# Revit family: 306_bb9c2a21bfbd4a688d0d3089b44ac4
name_source: partatom
category: Pipe Accessories
units: mm (PartAtom-declared; Revit-internal decimal feet)

## family parameters
Always vertical = Yes
Cut with Voids When Loaded = No
Part Type = Valve - Breaks Into
Round Connector Dimension = Use Diameter
Shared = No
Work Plane-Based = No

## types (8) — shared parameters
CAT0 = Yes
Description = 2-way Fan coil valve VLG122, PN16 external thread
E = 16 mm  [stored 0.0524934 ft]
H1 = 23 mm  [stored 0.0754593 ft]
L2D = 38 mm  [stored 0.124672 ft]
L2D_Min = 3048 mm  [stored 10 ft]
Manufacturer = ESBE
QmdConnectorList = 301;D;302;D
R10 = 8 mm  [stored 0.0262467 ft]
R3 = 4 mm  [stored 0.0131234 ft]
R4 = 6 mm
R5 = 7 mm  [stored 0.0229659 ft]
R8 = 2 mm  [stored 0.00656168 ft]
R9 = 9 mm  [stored 0.0295276 ft]
URL = http://www.esbe.eu
W2D = 15 mm  [stored 0.0492126 ft]
X4 = 7 mm  [stored 0.0229659 ft]
X4__ve = -7 mm  [stored -0.0229659 ft]
Z2 = 5 mm  [stored 0.0164042 ft]
Z3 = 2 mm  [stored 0.00656168 ft]
Z5 = 9 mm  [stored 0.0295276 ft]
Z7 = 3 mm  [stored 0.00984252 ft]
Z7__ve = -3 mm
Z8 = 4 mm  [stored 0.0131234 ft]
magiPartTypeId = 306
magiProductFamilyId = bb9c2a21bfbd4a688d0d3089b44ac4

## per-type parameters (varying)
| type | C | D | DT2 | H | LT2 | MC Product Code | R1 | R2 | R6 | R7 | X3 | Z1 | magiProductId |
| VLG122 PN16 15-0,25 G1/2 | 23 mm  [stored 0.0754593 ft] | 15 mm | 8 mm  [stored 0.0262467 ft] | 27 mm  [stored 0.0885827 ft] | 19 mm  [stored 0.062336 ft] | VLG122 PN16 15-0,25 G1/2" | 7 mm  [stored 0.0229659 ft] | 13 mm | 11 mm | 15 mm  [stored 0.0492126 ft] | 34 mm  [stored 0.111549 ft] | 3 mm  [stored 0.00984252 ft] | 6cccb35838dc4c688cd3b564d69ed3 |
| VLG122 PN16 15-0,4 G1/2 | 23 mm  [stored 0.0754593 ft] | 15 mm | 8 mm  [stored 0.0262467 ft] | 27 mm  [stored 0.0885827 ft] | 19 mm  [stored 0.062336 ft] | VLG122 PN16 15-0,4 G1/2" | 7 mm  [stored 0.0229659 ft] | 13 mm | 11 mm | 15 mm  [stored 0.0492126 ft] | 34 mm  [stored 0.111549 ft] | 3 mm  [stored 0.00984252 ft] | 3b824731ee3a4ddb922e904129e44f |
| VLG122 PN16 15-0,6 G1/2 | 23 mm  [stored 0.0754593 ft] | 15 mm | 8 mm  [stored 0.0262467 ft] | 27 mm  [stored 0.0885827 ft] | 19 mm  [stored 0.062336 ft] | VLG122 PN16 15-0,6 G1/2" | 7 mm  [stored 0.0229659 ft] | 13 mm | 11 mm | 15 mm  [stored 0.0492126 ft] | 34 mm  [stored 0.111549 ft] | 3 mm  [stored 0.00984252 ft] | f23e7b00549f42fba3d46801f33b4e |
| VLG122 PN16 15-1,0 G1/2 | 23 mm  [stored 0.0754593 ft] | 15 mm | 8 mm  [stored 0.0262467 ft] | 27 mm  [stored 0.0885827 ft] | 19 mm  [stored 0.062336 ft] | VLG122 PN16 15-1,0 G1/2" | 7 mm  [stored 0.0229659 ft] | 13 mm | 11 mm | 15 mm  [stored 0.0492126 ft] | 34 mm  [stored 0.111549 ft] | 3 mm  [stored 0.00984252 ft] | 8756f888f78f4439910ff664cb444d |
| VLG122 PN16 15-1,6 G1/2 | 23 mm  [stored 0.0754593 ft] | 15 mm | 8 mm  [stored 0.0262467 ft] | 27 mm  [stored 0.0885827 ft] | 19 mm  [stored 0.062336 ft] | VLG122 PN16 15-1,6 G1/2" | 7 mm  [stored 0.0229659 ft] | 13 mm | 11 mm | 15 mm  [stored 0.0492126 ft] | 34 mm  [stored 0.111549 ft] | 3 mm  [stored 0.00984252 ft] | 5de91fdcf4d14890add016a982ef49 |
| VLG122 PN16 20-2,5 G3/4 | 24 mm  [stored 0.0787402 ft] | 20 mm | 10 mm  [stored 0.0328084 ft] | 26 mm  [stored 0.0853018 ft] | 21 mm  [stored 0.0688976 ft] | VLG122 PN16 20-2,5 G3/4" | 9 mm  [stored 0.0295276 ft] | 15 mm  [stored 0.0492126 ft] | 12 mm  [stored 0.0393701 ft] | 16 mm  [stored 0.0524934 ft] | 38 mm  [stored 0.124672 ft] | 4 mm  [stored 0.0131234 ft] | 3d202c79ad1e46bdb67021412b49dc |
| VLG122 PN16 20-4,0 G3/4 | 24 mm  [stored 0.0787402 ft] | 20 mm | 10 mm  [stored 0.0328084 ft] | 26 mm  [stored 0.0853018 ft] | 21 mm  [stored 0.0688976 ft] | VLG122 PN16 20-4,0 G3/4" | 9 mm  [stored 0.0295276 ft] | 15 mm  [stored 0.0492126 ft] | 12 mm  [stored 0.0393701 ft] | 16 mm  [stored 0.0524934 ft] | 38 mm  [stored 0.124672 ft] | 4 mm  [stored 0.0131234 ft] | aeef4dbbb471400997988208d80840 |
| VLG122 PN16 20-6,0 G3/4 | 24 mm  [stored 0.0787402 ft] | 20 mm | 10 mm  [stored 0.0328084 ft] | 26 mm  [stored 0.0853018 ft] | 21 mm  [stored 0.0688976 ft] | VLG122 PN16 20-6,0 G3/4" | 9 mm  [stored 0.0295276 ft] | 15 mm  [stored 0.0492126 ft] | 12 mm  [stored 0.0393701 ft] | 16 mm  [stored 0.0524934 ft] | 38 mm  [stored 0.124672 ft] | 4 mm  [stored 0.0131234 ft] | d50cdf1684844ef7b6c9e5ea35d552 |

note: [stored X ft] marks values corroborated as IEEE doubles in the binary element streams (Revit-internal decimal feet)
